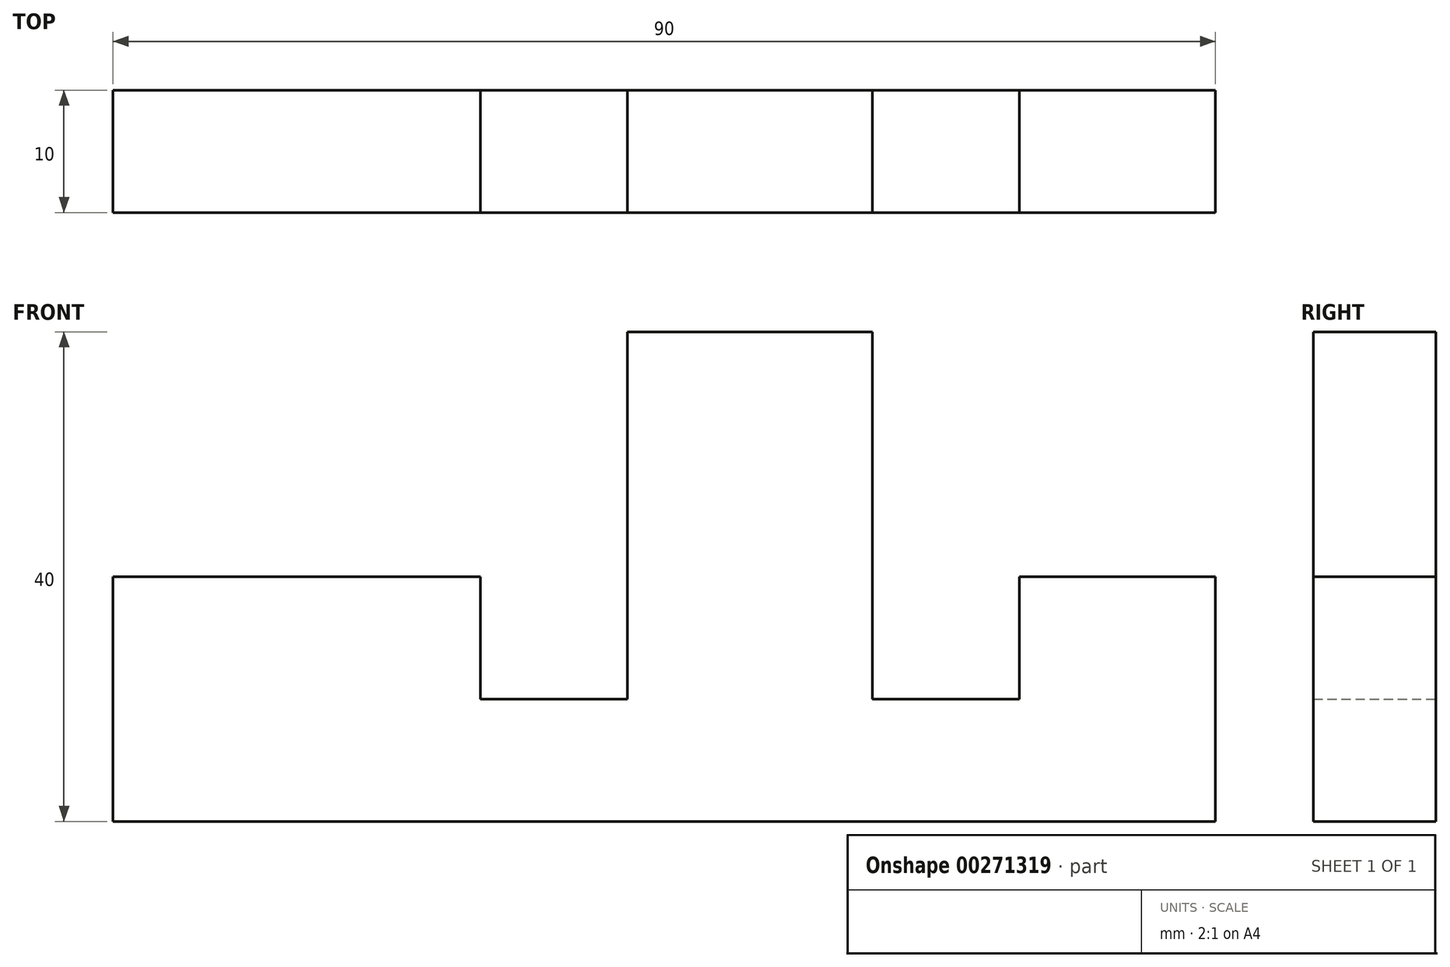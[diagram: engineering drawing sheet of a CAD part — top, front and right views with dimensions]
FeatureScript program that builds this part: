
annotation { "Feature Type Name" : "Feature", "Feature Type Description" : "" }
export const myFeature = defineFeature(function(context is Context, id is Id, definition is map)
    precondition{}
    {
        {
            var Q0;
            Q0=qCreatedBy(makeId("Front.planeOp"),FACE);
            var sketch = newSketch(context, id + "F0", { "sketchPlane" : qUnion([Q0])});
            skLineSegment(sketch, "E0", {"start": v(0, 0) * mm, "end": v(90, 0) * mm});
            skLineSegment(sketch, "E1", {"start": v(0, 0) * mm, "end": v(0, 20) * mm});
            skLineSegment(sketch, "E2", {"start": v(30, 20) * mm, "end": v(30, 10) * mm});
            skLineSegment(sketch, "E3", {"start": v(30, 10) * mm, "end": v(42, 10) * mm});
            skLineSegment(sketch, "E4", {"start": v(42, 10) * mm, "end": v(42, 40) * mm});
            skLineSegment(sketch, "E5", {"start": v(42, 40) * mm, "end": v(62, 40) * mm});
            skLineSegment(sketch, "E6", {"start": v(62, 40) * mm, "end": v(62, 10) * mm});
            skLineSegment(sketch, "E7", {"start": v(62, 10) * mm, "end": v(74, 10) * mm});
            skLineSegment(sketch, "E8", {"start": v(74, 10) * mm, "end": v(74, 20) * mm});
            skLineSegment(sketch, "E9", {"start": v(74, 20) * mm, "end": v(90, 20) * mm});
            skLineSegment(sketch, "E10", {"start": v(90, 20) * mm, "end": v(90, 0) * mm});
            skLineSegment(sketch, "E11", {"start": v(0, 20) * mm, "end": v(30, 20) * mm});
            skSolve(sketch);
        }
        {
            var Q0;
            Q0 = qSketchRegion(id + "F0", true);
            extrude(context, id + "F1", {"entities" : qUnion([Q0]), "depth" : 10 * mm});
        }
    });
